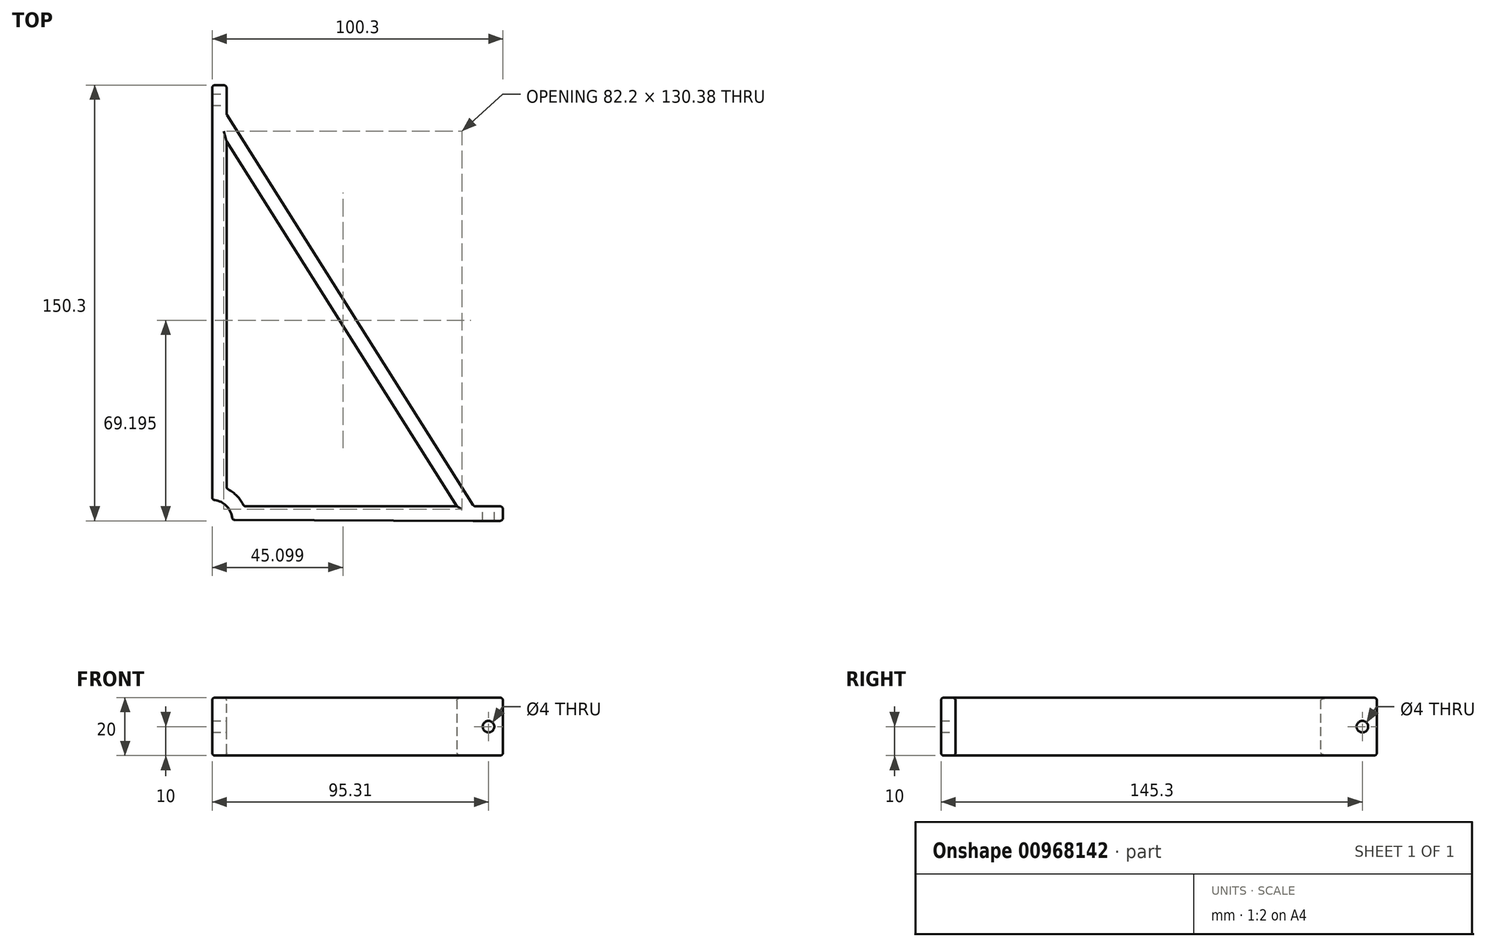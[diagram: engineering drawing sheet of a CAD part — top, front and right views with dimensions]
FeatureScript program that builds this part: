
annotation { "Feature Type Name" : "Feature", "Feature Type Description" : "" }
export const myFeature = defineFeature(function(context is Context, id is Id, definition is map)
    precondition{}
    {
        {
            var Q0;
            Q0=qCreatedBy(makeId("Top.planeOp"),FACE);
            var sketch = newSketch(context, id + "F0", { "sketchPlane" : qUnion([Q0])});
            skLineSegment(sketch, "E0", {"start": v(90.3, 4.7) * mm, "end": v(10.96, 4.7) * mm});
            skLineSegment(sketch, "E1", {"start": v(5, 140) * mm, "end": v(5, 150) * mm});
            skLineSegment(sketch, "E2", {"start": v(5, 140) * mm, "end": v(90.3, 4.7) * mm});
            skLineSegment(sketch, "E3", {"start": v(5, 130.62) * mm, "end": v(84.38, 4.7) * mm});
            skLineSegment(sketch, "E4", {"start": v(48.83, 70.47) * mm, "end": v(44.6, 67.8) * mm, "construction": true});
            skPoint(sketch, "E5.visualSharp", {"position": v(0, 0) * mm});
            skLineSegment(sketch, "E6.bottom", {"start": v(90.3, 4.7) * mm, "end": v(100.3, 4.7) * mm});
            skLineSegment(sketch, "E6.right", {"start": v(100.3, 4.7) * mm, "end": v(100.3, -0.3) * mm});
            skLineSegment(sketch, "E7", {"start": v(0, 150) * mm, "end": v(5, 150) * mm});
            skLineSegment(sketch, "E8", {"start": v(90, -0.3) * mm, "end": v(6.93, -0.02) * mm});
            skLineSegment(sketch, "E9", {"start": v(90, -0.3) * mm, "end": v(100.3, -0.3) * mm});
            skLineSegment(sketch, "E10", {"start": v(0, 150) * mm, "end": v(0, 6.93) * mm});
            skPoint(sketch, "E11", {"position": v(0, 6.93) * mm});
            skPoint(sketch, "E12", {"position": v(0, 11.93) * mm});
            skPoint(sketch, "E13", {"position": v(6.93, -0.02) * mm});
            skPoint(sketch, "E14", {"position": v(11.93, -0.04) * mm});
            skPoint(sketch, "E15", {"position": v(10.96, 4.7) * mm});
            skPoint(sketch, "E16", {"position": v(5, 10.83) * mm});
            skArc(sketch, "E17", {"start": v(10.96, 4.7) * mm, "mid": v(8.55, 8.32) * mm, "end": v(5, 10.83) * mm});
            skLineSegment(sketch, "E18", {"start": v(0, 6.93) * mm, "end": v(0, 6.93) * mm});
            skLineSegment(sketch, "E19", {"start": v(6.93, -0.02) * mm, "end": v(6.93, -0.02) * mm});
            skArc(sketch, "E20", {"start": v(6.93, -0.02) * mm, "mid": v(4.9, 4.89) * mm, "end": v(0, 6.93) * mm});
            skLineSegment(sketch, "E21", {"start": v(5, 10.83) * mm, "end": v(5, 140) * mm});
            skSolve(sketch);
        }
        {
            var Q0;
            Q0=makeQuery(id+"F0.imprint","IMPRINT",FACE,{"disambiguationData":[TD([[makeQuery(id+"F0.imprint","IMPRINT",EDGE,{"derivedFrom":sQuery(id+"F0.wireOp",EDGE,"n3vvUF1v-HjJq-pRef-TAmz-BCNGJ9hifS0P")}),1.0]])]});
            var Q1;
            Q1=makeQuery(id+"F0.imprint","IMPRINT",FACE,{"disambiguationData":[TD([[makeQuery(id+"F0.imprint","IMPRINT",EDGE,{"derivedFrom":sQuery(id+"F0.wireOp",EDGE,"L6S9Jzb9-e6Hn-Th6M-tdlC-rLtljIUr4Bqt")}),1.0]])]});
            var Q2;
            {var subQ0=sQuery(id+"F0.wireOp",EDGE,"E2");Q2=makeQuery(id+"F0.imprint","IMPRINT",FACE,{"disambiguationData":[TD([[makeQuery(id+"F0.imprint","IMPRINT",EDGE,{"derivedFrom":subQ0}),-1.0]])]});}
            var Q3;
            Q3=makeQuery(id+"F0.imprint","IMPRINT",FACE,{"disambiguationData":[TD([[makeQuery(id+"F0.imprint","IMPRINT",EDGE,{"derivedFrom":sQuery(id+"F0.wireOp",EDGE,"roJCYxsm-ZAQD-ukU0-9hnD-tYJg5mqca81K")}),1.0]])]});
            var Q4;
            Q4=makeQuery(id+"F0.imprint","IMPRINT",FACE,{"disambiguationData":[TD([[makeQuery(id+"F0.imprint","IMPRINT",EDGE,{"derivedFrom":sQuery(id+"F0.wireOp",EDGE,"E6.bottom")}),-1.0]])]});
            extrude(context, id + "F1", {"entities" : qUnion([Q0, Q1, Q2, Q3, Q4]), "depth" : 20 * mm, "offsetDistance" : 25 * mm});
        }
        {
            var Q0;
            Q0=makeQuery(id+"F1.opExtrude","SWEPT_FACE",FACE,{"disambiguationData":[OSD([sQuery(id+"F0.wireOp",EDGE,"E1")])]});
            var sketch = newSketch(context, id + "F2", { "sketchPlane" : qUnion([Q0])});
            skCircle(sketch, "E22", {"center": v(145, 10) * mm, "radius": 2 * mm});
            skLineSegment(sketch, "E23", {"start": v(145, 10) * mm, "end": v(150, 10) * mm, "construction": true});
            skLineSegment(sketch, "E24", {"start": v(145, 10) * mm, "end": v(140, 10) * mm, "construction": true});
            skLineSegment(sketch, "E25", {"start": v(145, 10) * mm, "end": v(145, 20) * mm, "construction": true});
            skLineSegment(sketch, "E26", {"start": v(145, 10) * mm, "end": v(145, 0) * mm, "construction": true});
            skSolve(sketch);
        }
        {
            var Q0;
            Q0=makeQuery(id+"F2.imprint","IMPRINT",FACE,{"disambiguationData":[TD([[makeQuery(id+"F2.imprint","IMPRINT",EDGE,{"derivedFrom":sQuery(id+"F2.wireOp",EDGE,"E22")}),1.0]])]});
            extrude(context, id + "F3", {"entities" : qUnion([Q0]), "operationType" : NewBodyOperationType.REMOVE, "oppositeDirection" : true, "depth" : 25 * mm, "offsetDistance" : 25 * mm});
        }
        {
            var Q0;
            Q0=makeQuery(id+"F1.opExtrude","SWEPT_FACE",FACE,{"disambiguationData":[OSD([sQuery(id+"F0.wireOp",EDGE,"E0")])]});
            var sketch = newSketch(context, id + "F4", { "sketchPlane" : qUnion([Q0])});
            skCircle(sketch, "E27", {"center": v(-95.3, 10) * mm, "radius": 2 * mm});
            skCircle(sketch, "E28.0", {"center": v(-95.3, 10) * mm, "radius": 5 * mm});
            skLineSegment(sketch, "E29", {"start": v(-95.3, 20) * mm, "end": v(-95.3, 10) * mm, "construction": true});
            skLineSegment(sketch, "E30", {"start": v(-95.3, 0) * mm, "end": v(-95.3, 10) * mm, "construction": true});
            skSolve(sketch);
        }
        {
            var Q0;
            Q0=makeQuery(id+"F4.imprint","IMPRINT",FACE,{"disambiguationData":[TD([[makeQuery(id+"F4.imprint","IMPRINT",EDGE,{"derivedFrom":sQuery(id+"F4.wireOp",EDGE,"E27")}),1.0]])]});
            extrude(context, id + "F5", {"entities" : qUnion([Q0]), "operationType" : NewBodyOperationType.REMOVE, "oppositeDirection" : true, "depth" : 25 * mm, "offsetDistance" : 25 * mm});
        }
        {
            var Q0;
            Q0=makeQuery(id+"F1.opExtrude","SWEPT_EDGE",EDGE,{"disambiguationData":[OSD([sQuery(id+"F0.wireOp",EDGE,"E6.bottom"),sQuery(id+"F0.wireOp",EDGE,"E6.right")])]});
            var Q1;
            Q1=makeQuery(id+"F1.opExtrude","CAP_FACE",FACE,{"disambiguationData":[OSD([sQuery(id+"F0.wireOp",EDGE,"1y2EyMIw-ggku-gnqF-ws5w-DgIzufdhCj6A"),sQuery(id+"F0.wireOp",EDGE,"E0"),sQuery(id+"F0.wireOp",EDGE,"vfPcvNVu-cdJS-rE6l-kH6c-c8hAMcQBhuOQ"),sQuery(id+"F0.wireOp",EDGE,"BxpMXeKD-ChcD-UC1l-BN9b-5ZePUrebT5EE"),sQuery(id+"F0.wireOp",EDGE,"E1"),sQuery(id+"F0.wireOp",EDGE,"E2"),sQuery(id+"F0.wireOp",EDGE,"E3"),sQuery(id+"F0.wireOp",EDGE,"roJCYxsm-ZAQD-ukU0-9hnD-tYJg5mqca81K"),sQuery(id+"F0.wireOp",EDGE,"E6.bottom"),sQuery(id+"F0.wireOp",EDGE,"E6.top"),sQuery(id+"F0.wireOp",EDGE,"E6.right"),sQuery(id+"F0.wireOp",EDGE,"E7"),sQuery(id+"F0.wireOp",EDGE,"E8")])],"isStart":false});
            var Q2;
            Q2=makeQuery(id+"F1.opExtrude","CAP_FACE",FACE,{"disambiguationData":[OSD([sQuery(id+"F0.wireOp",EDGE,"1y2EyMIw-ggku-gnqF-ws5w-DgIzufdhCj6A"),sQuery(id+"F0.wireOp",EDGE,"E0"),sQuery(id+"F0.wireOp",EDGE,"vfPcvNVu-cdJS-rE6l-kH6c-c8hAMcQBhuOQ"),sQuery(id+"F0.wireOp",EDGE,"BxpMXeKD-ChcD-UC1l-BN9b-5ZePUrebT5EE"),sQuery(id+"F0.wireOp",EDGE,"E1"),sQuery(id+"F0.wireOp",EDGE,"E2"),sQuery(id+"F0.wireOp",EDGE,"E3"),sQuery(id+"F0.wireOp",EDGE,"roJCYxsm-ZAQD-ukU0-9hnD-tYJg5mqca81K"),sQuery(id+"F0.wireOp",EDGE,"E6.bottom"),sQuery(id+"F0.wireOp",EDGE,"E6.top"),sQuery(id+"F0.wireOp",EDGE,"E6.right"),sQuery(id+"F0.wireOp",EDGE,"E7"),sQuery(id+"F0.wireOp",EDGE,"E8")])],"isStart":true});
            var Q3;
            Q3=makeQuery(id+"F1.opExtrude","SWEPT_EDGE",EDGE,{"disambiguationData":[OSD([sQuery(id+"F0.wireOp",EDGE,"E6.top"),sQuery(id+"F0.wireOp",EDGE,"E6.right")])]});
            var Q4;
            Q4=makeQuery(id+"F3.boolean.opBoolean","COPY",EDGE,{"derivedFrom":makeQuery(id+"F3.opExtrude","CAP_EDGE",EDGE,{"disambiguationData":[OSD([sQuery(id+"F2.wireOp",EDGE,"E22")])],"isStart":true})});
            var Q5;
            Q5=makeQuery(id+"F5.boolean.opBoolean","COPY",EDGE,{"derivedFrom":makeQuery(id+"F5.opExtrude","CAP_EDGE",EDGE,{"disambiguationData":[OSD([sQuery(id+"F4.wireOp",EDGE,"E27")])],"isStart":true})});
            var Q6;
            Q6=makeQuery(id+"F1.opExtrude","SWEPT_EDGE",EDGE,{"disambiguationData":[OSD([sQuery(id+"F0.wireOp",EDGE,"E0"),sQuery(id+"F0.wireOp",EDGE,"E2"),sQuery(id+"F0.wireOp",EDGE,"E6.bottom"),sQuery(id+"F0.wireOp",EDGE,"E6.left")])]});
            var Q7;
            Q7=makeQuery(id+"F1.opExtrude","SWEPT_EDGE",EDGE,{"disambiguationData":[OSD([sQuery(id+"F0.wireOp",EDGE,"vfPcvNVu-cdJS-rE6l-kH6c-c8hAMcQBhuOQ"),sQuery(id+"F0.wireOp",EDGE,"E1"),sQuery(id+"F0.wireOp",EDGE,"E2")])]});
            var Q8;
            Q8=makeQuery(id+"F1.opExtrude","SWEPT_EDGE",EDGE,{"disambiguationData":[OSD([sQuery(id+"F0.wireOp",EDGE,"E1"),sQuery(id+"F0.wireOp",EDGE,"E7")])]});
            var Q9;
            Q9=makeQuery(id+"F1.opExtrude","SWEPT_EDGE",EDGE,{"disambiguationData":[OSD([sQuery(id+"F0.wireOp",EDGE,"BxpMXeKD-ChcD-UC1l-BN9b-5ZePUrebT5EE"),sQuery(id+"F0.wireOp",EDGE,"E7")])]});
            var Q10;
            Q10=makeQuery(id+"F1.opExtrude","SWEPT_EDGE",EDGE,{"disambiguationData":[OSD([sQuery(id+"F0.wireOp",EDGE,"E8"),sQuery(id+"F0.wireOp",EDGE,"E20")])]});
            var Q11;
            Q11=makeQuery(id+"F1.opExtrude","SWEPT_EDGE",EDGE,{"disambiguationData":[OSD([sQuery(id+"F0.wireOp",EDGE,"E10"),sQuery(id+"F0.wireOp",EDGE,"E20")])]});
            var Q12;
            Q12=makeQuery(id+"F1.opExtrude","SWEPT_EDGE",EDGE,{"disambiguationData":[OSD([sQuery(id+"F0.wireOp",EDGE,"E17"),sQuery(id+"F0.wireOp",EDGE,"E21")])]});
            var Q13;
            Q13=makeQuery(id+"F1.opExtrude","SWEPT_EDGE",EDGE,{"disambiguationData":[OSD([sQuery(id+"F0.wireOp",EDGE,"E0"),sQuery(id+"F0.wireOp",EDGE,"E17")])]});
            fillet(context, id + "F6", {"entities" : qUnion([Q0, Q1, Q2, Q3, Q4, Q5, Q6, Q7, Q8, Q9, Q10, Q11, Q12, Q13]), "radius" : 1 * mm, "tangentPropagation" : true, "allowEdgeOverflow" : false});
        }
    });
